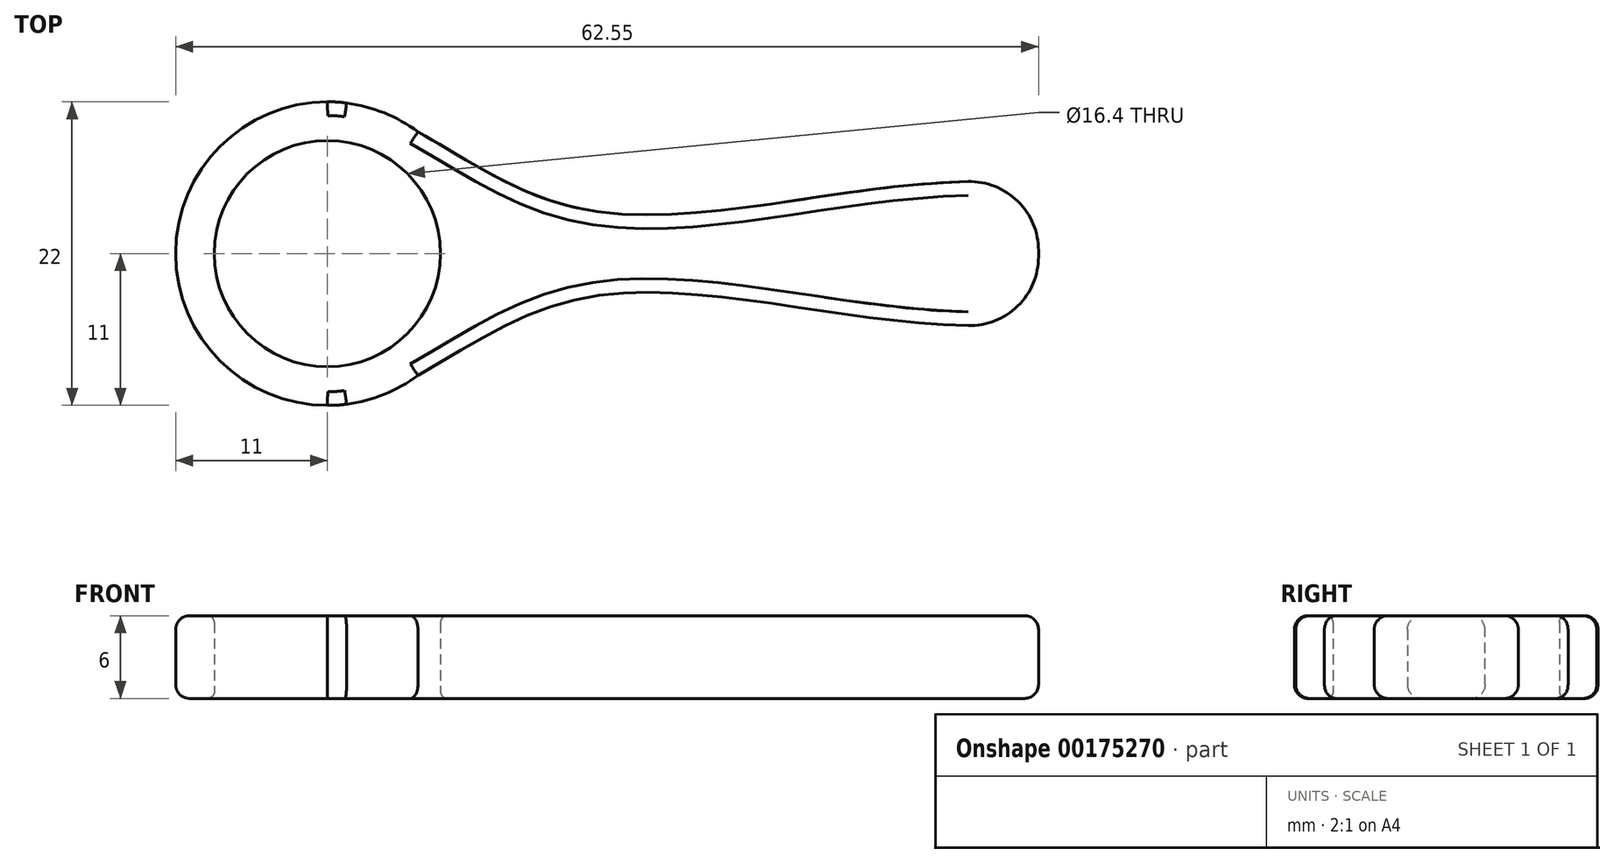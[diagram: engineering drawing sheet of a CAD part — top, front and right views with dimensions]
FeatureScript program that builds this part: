
annotation { "Feature Type Name" : "Feature", "Feature Type Description" : "" }
export const myFeature = defineFeature(function(context is Context, id is Id, definition is map)
    precondition{}
    {
        {
            var Q0;
            Q0=qCreatedBy(makeId("Top.planeOp"),FACE);
            var sketch = newSketch(context, id + "F0", { "sketchPlane" : qUnion([Q0])});
            skCircle(sketch, "E0", {"center": v(0, 0) * mm, "radius": 8.2 * mm});
            skCircle(sketch, "E1", {"center": v(0, 0) * mm, "radius": 11 * mm});
            skLineSegment(sketch, "E2", {"start": v(51.55, 5) * mm, "end": v(51.55, -5) * mm});
            skFitSpline(sketch, "E3", {"points": [v(0, -11) * mm, v(17.7, -3.4) * mm, v(51.55, -5) * mm], "startDerivative": vector(36.28, -1.37) * mm, "endDerivative": vector(60.97, 7.22) * mm});
            skFitSpline(sketch, "E4.MirrorCS", {"points": [v(0, 11) * mm, v(17.7, 3.4) * mm, v(51.55, 5) * mm], "startDerivative": vector(36.28, 1.37) * mm, "endDerivative": vector(60.97, -7.22) * mm});
            skSolve(sketch);
        }
        {
            var Q0;
            Q0=qSketchRegion(id+"F0",true);
            extrude(context, id + "F1", {"entities" : qUnion([Q0]), "depth" : 6 * mm});
        }
        {
            var Q0;
            Q0=makeQuery(id+"F1.opExtrude","SWEPT_EDGE",EDGE,{"disambiguationData":[OSD([sQuery(id+"F0.wireOp",EDGE,"E2"),sQuery(id+"F0.wireOp",EDGE,"LiMI4g3x-Ub7L-HzqR-8dG1-9Mk6N0thp5We")])]});
            var Q1;
            Q1=makeQuery(id+"F1.opExtrude","SWEPT_EDGE",EDGE,{"disambiguationData":[OSD([sQuery(id+"F0.wireOp",EDGE,"KogE2yOf-XQ3Q-wfs9-vSaF-3sXPLG2ve2sv"),sQuery(id+"F0.wireOp",EDGE,"E2")])]});
            fillet(context, id + "F2", {"entities" : qUnion([Q0, Q1]), "radius" : 5 * mm, "tangentPropagation" : true, "allowEdgeOverflow" : false});
        }
        {
            var Q0;
            Q0=makeQuery(id+"F1.opExtrude","CAP_EDGE",EDGE,{"disambiguationData":[OSD([sQuery(id+"F0.wireOp",EDGE,"E1")])],"isStart":false});
            var Q1;
            Q1=makeQuery(id+"F1.opExtrude","CAP_EDGE",EDGE,{"disambiguationData":[OSD([sQuery(id+"F0.wireOp",EDGE,"KogE2yOf-XQ3Q-wfs9-vSaF-3sXPLG2ve2sv")])],"isStart":false});
            var Q2;
            Q2=makeQuery(id+"F1.opExtrude","CAP_EDGE",EDGE,{"disambiguationData":[OSD([sQuery(id+"F0.wireOp",EDGE,"LiMI4g3x-Ub7L-HzqR-8dG1-9Mk6N0thp5We")])],"isStart":false});
            var Q3;
            {var subQ0=sQuery(id+"F0.wireOp",EDGE,"LiMI4g3x-Ub7L-HzqR-8dG1-9Mk6N0thp5We");var subQ1=sQuery(id+"F0.wireOp",EDGE,"E2");Q3=makeQuery(id+"F2.opFillet","BLEND_EDGE",EDGE,{"blendedFrom":[makeQuery(id+"F1.opExtrude","SWEPT_EDGE",EDGE,{"disambiguationData":[OSD([subQ1,subQ0])]}),makeQuery(id+"F1.opExtrude","CAP_FACE",FACE,{"disambiguationData":[OSD([sQuery(id+"F0.wireOp",EDGE,"E0"),sQuery(id+"F0.wireOp",EDGE,"E1"),sQuery(id+"F0.wireOp",EDGE,"KogE2yOf-XQ3Q-wfs9-vSaF-3sXPLG2ve2sv"),subQ1,subQ0])],"isStart":false})],"blendedInto":[makeQuery(id+"F1.opExtrude","CAP_FACE",FACE,{"disambiguationData":[OSD([sQuery(id+"F0.wireOp",EDGE,"E0"),sQuery(id+"F0.wireOp",EDGE,"E1"),sQuery(id+"F0.wireOp",EDGE,"KogE2yOf-XQ3Q-wfs9-vSaF-3sXPLG2ve2sv"),subQ1,subQ0])],"isStart":false})]});}
            var Q4;
            {var subQ0=sQuery(id+"F0.wireOp",EDGE,"E2");var subQ1=sQuery(id+"F0.wireOp",EDGE,"KogE2yOf-XQ3Q-wfs9-vSaF-3sXPLG2ve2sv");Q4=makeQuery(id+"F2.opFillet","BLEND_EDGE",EDGE,{"blendedFrom":[makeQuery(id+"F1.opExtrude","SWEPT_EDGE",EDGE,{"disambiguationData":[OSD([subQ1,subQ0])]}),makeQuery(id+"F1.opExtrude","CAP_FACE",FACE,{"disambiguationData":[OSD([sQuery(id+"F0.wireOp",EDGE,"E0"),sQuery(id+"F0.wireOp",EDGE,"E1"),subQ1,subQ0,sQuery(id+"F0.wireOp",EDGE,"LiMI4g3x-Ub7L-HzqR-8dG1-9Mk6N0thp5We")])],"isStart":false})],"blendedInto":[makeQuery(id+"F1.opExtrude","CAP_FACE",FACE,{"disambiguationData":[OSD([sQuery(id+"F0.wireOp",EDGE,"E0"),sQuery(id+"F0.wireOp",EDGE,"E1"),subQ1,subQ0,sQuery(id+"F0.wireOp",EDGE,"LiMI4g3x-Ub7L-HzqR-8dG1-9Mk6N0thp5We")])],"isStart":false})]});}
            var Q5;
            Q5=makeQuery(id+"F1.opExtrude","CAP_EDGE",EDGE,{"disambiguationData":[OSD([sQuery(id+"F0.wireOp",EDGE,"E1")])],"isStart":true});
            var Q6;
            Q6=makeQuery(id+"F1.opExtrude","CAP_EDGE",EDGE,{"disambiguationData":[OSD([sQuery(id+"F0.wireOp",EDGE,"LiMI4g3x-Ub7L-HzqR-8dG1-9Mk6N0thp5We")])],"isStart":true});
            var Q7;
            {var subQ0=sQuery(id+"F0.wireOp",EDGE,"LiMI4g3x-Ub7L-HzqR-8dG1-9Mk6N0thp5We");var subQ1=sQuery(id+"F0.wireOp",EDGE,"E2");Q7=makeQuery(id+"F2.opFillet","BLEND_EDGE",EDGE,{"blendedFrom":[makeQuery(id+"F1.opExtrude","SWEPT_EDGE",EDGE,{"disambiguationData":[OSD([subQ1,subQ0])]}),makeQuery(id+"F1.opExtrude","CAP_FACE",FACE,{"disambiguationData":[OSD([sQuery(id+"F0.wireOp",EDGE,"E0"),sQuery(id+"F0.wireOp",EDGE,"E1"),sQuery(id+"F0.wireOp",EDGE,"KogE2yOf-XQ3Q-wfs9-vSaF-3sXPLG2ve2sv"),subQ1,subQ0])],"isStart":true})],"blendedInto":[makeQuery(id+"F1.opExtrude","CAP_FACE",FACE,{"disambiguationData":[OSD([sQuery(id+"F0.wireOp",EDGE,"E0"),sQuery(id+"F0.wireOp",EDGE,"E1"),sQuery(id+"F0.wireOp",EDGE,"KogE2yOf-XQ3Q-wfs9-vSaF-3sXPLG2ve2sv"),subQ1,subQ0])],"isStart":true})]});}
            var Q8;
            {var subQ0=sQuery(id+"F0.wireOp",EDGE,"E2");var subQ1=sQuery(id+"F0.wireOp",EDGE,"KogE2yOf-XQ3Q-wfs9-vSaF-3sXPLG2ve2sv");Q8=makeQuery(id+"F2.opFillet","BLEND_EDGE",EDGE,{"blendedFrom":[makeQuery(id+"F1.opExtrude","SWEPT_EDGE",EDGE,{"disambiguationData":[OSD([subQ1,subQ0])]}),makeQuery(id+"F1.opExtrude","CAP_FACE",FACE,{"disambiguationData":[OSD([sQuery(id+"F0.wireOp",EDGE,"E0"),sQuery(id+"F0.wireOp",EDGE,"E1"),subQ1,subQ0,sQuery(id+"F0.wireOp",EDGE,"LiMI4g3x-Ub7L-HzqR-8dG1-9Mk6N0thp5We")])],"isStart":true})],"blendedInto":[makeQuery(id+"F1.opExtrude","CAP_FACE",FACE,{"disambiguationData":[OSD([sQuery(id+"F0.wireOp",EDGE,"E0"),sQuery(id+"F0.wireOp",EDGE,"E1"),subQ1,subQ0,sQuery(id+"F0.wireOp",EDGE,"LiMI4g3x-Ub7L-HzqR-8dG1-9Mk6N0thp5We")])],"isStart":true})]});}
            var Q9;
            Q9=makeQuery(id+"F1.opExtrude","CAP_EDGE",EDGE,{"disambiguationData":[OSD([sQuery(id+"F0.wireOp",EDGE,"KogE2yOf-XQ3Q-wfs9-vSaF-3sXPLG2ve2sv")])],"isStart":true});
            fillet(context, id + "F3", {"entities" : qUnion([Q0, Q1, Q2, Q3, Q4, Q5, Q6, Q7, Q8, Q9]), "radius" : 1 * mm, "tangentPropagation" : true, "allowEdgeOverflow" : false});
        }
        {
            var Q0;
            Q0=makeQuery(id+"F1.opExtrude","CAP_EDGE",EDGE,{"disambiguationData":[OSD([sQuery(id+"F0.wireOp",EDGE,"E0")])],"isStart":true});
            fillet(context, id + "F4", {"entities" : qUnion([Q0]), "radius" : 0.5 * mm, "tangentPropagation" : true, "allowEdgeOverflow" : false});
        }
        {
            var Q0;
            Q0=makeQuery(id+"F1.opExtrude","CAP_EDGE",EDGE,{"disambiguationData":[OSD([sQuery(id+"F0.wireOp",EDGE,"E0")])],"isStart":false});
            fillet(context, id + "F5", {"entities" : qUnion([Q0]), "radius" : 0.5 * mm, "tangentPropagation" : true, "allowEdgeOverflow" : false});
        }
    });
